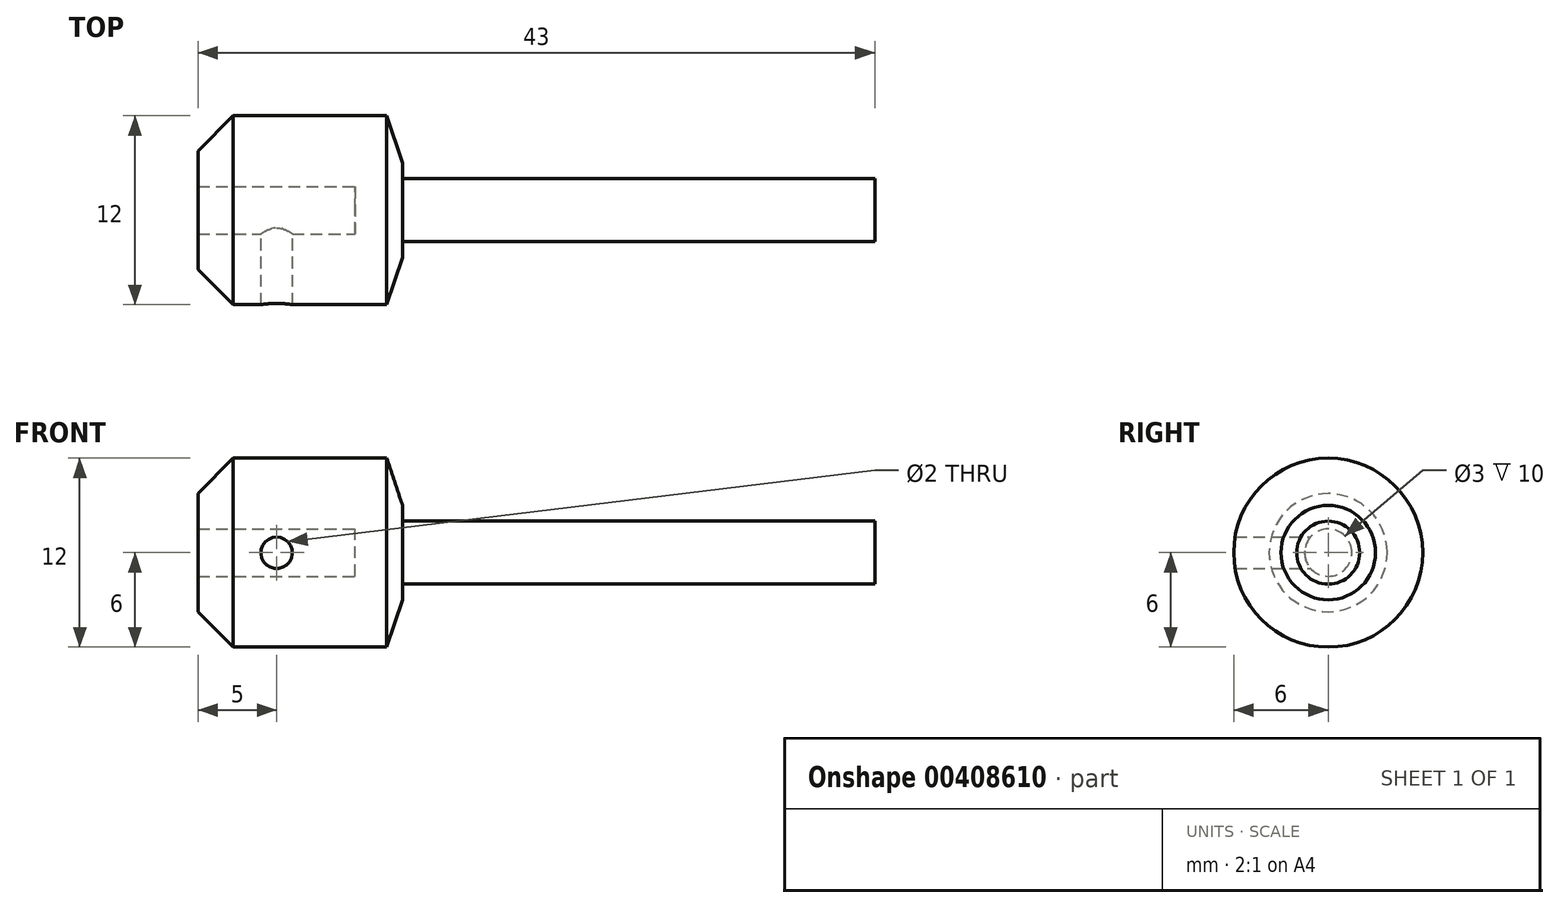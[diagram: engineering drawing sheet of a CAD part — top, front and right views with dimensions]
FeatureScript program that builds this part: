
annotation { "Feature Type Name" : "Feature", "Feature Type Description" : "" }
export const myFeature = defineFeature(function(context is Context, id is Id, definition is map)
    precondition{}
    {
        {
            var Q0;
            Q0=qCreatedBy(makeId("Front.planeOp"),FACE);
            var sketch = newSketch(context, id + "F0", { "sketchPlane" : qUnion([Q0])});
            skLineSegment(sketch, "E0", {"start": v(0, 0) * mm, "end": v(-33, 0) * mm});
            skLineSegment(sketch, "E1", {"start": v(-33, 0) * mm, "end": v(-33, 1.5) * mm});
            skLineSegment(sketch, "E2", {"start": v(-33, 1.5) * mm, "end": v(-43, 1.5) * mm});
            skLineSegment(sketch, "E3", {"start": v(-43, 1.5) * mm, "end": v(-43, 3.75) * mm});
            skLineSegment(sketch, "E4", {"start": v(-40.75, 6) * mm, "end": v(-30, 6) * mm});
            skLineSegment(sketch, "E5", {"start": v(-30, 6) * mm, "end": v(-30, 2) * mm});
            skLineSegment(sketch, "E6", {"start": v(-30, 2) * mm, "end": v(0, 2) * mm});
            skLineSegment(sketch, "E7", {"start": v(0, 2) * mm, "end": v(0, 0) * mm});
            skLineSegment(sketch, "E8", {"start": v(-43, 3.75) * mm, "end": v(-40.75, 6) * mm});
            skPoint(sketch, "E9.orphan", {"position": v(-43, 6) * mm});
            skSolve(sketch);
        }
        {
            var Q0;
            Q0 = qSketchRegion(id + "F0", true);
            var Q1;
            Q1=sQuery(id+"F0.wireOp",EDGE,"E0");
            revolve(context, id + "F1", {"entities" : qUnion([Q0]), "axis" : qUnion([Q1]), "revolveType" : RevolveType.FULL});
        }
        {
            var Q0;
            Q0=qCreatedBy(makeId("Front.planeOp"),FACE);
            var sketch = newSketch(context, id + "F2", { "sketchPlane" : qUnion([Q0])});
            skCircle(sketch, "E10", {"center": v(-38, 0) * mm, "radius": 1 * mm});
            skSolve(sketch);
        }
        {
            var Q0;
            Q0 = qSketchRegion(id + "F2", true);
            extrude(context, id + "F3", {"entities" : qUnion([Q0]), "operationType" : NewBodyOperationType.REMOVE, "depth" : 10 * mm});
        }
        {
            var Q0;
            Q0=makeQuery(id+"F1.opRevolve","SWEPT_EDGE",EDGE,{"disambiguationData":[OSD([sQuery(id+"F0.wireOp",EDGE,"E4"),sQuery(id+"F0.wireOp",EDGE,"E5")])]});
            chamfer(context, id + "F4", {"entities" : qUnion([Q0]), "chamferType" : ChamferType.TWO_OFFSETS, "width1" : 3 * mm, "oppositeDirection" : false, "width2" : 1 * mm, "tangentPropagation" : true});
        }
    });
